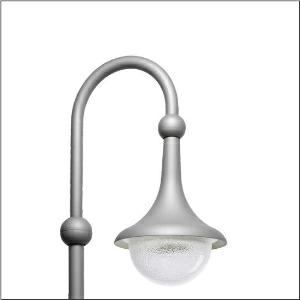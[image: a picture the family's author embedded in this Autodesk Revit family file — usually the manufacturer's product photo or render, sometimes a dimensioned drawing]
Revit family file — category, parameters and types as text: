
# Revit family: kleine_glocke___st1_2a_5xa1573k1b208_586f
name_source: partatom
category: Lighting Fixtures
units: mm (PartAtom-declared; Revit-internal decimal feet)

## family parameters
Cut with Voids When Loaded = No
Host = Face
Light Source = No
Part Type = Normal
Room Calculation Point = No
Round Connector Dimension = Use Diameter
Shared = No

## types (1)
- --- (1 x LED, 1750 lm, 13.2 W, 4000K)
    Apparent Load = 13 VA
    CIE Flux Codes = 28 64 93 98 100
    Color Rendering = 70
    Color Temperature = 4000K
    Default Elevation = 1800 mm
    Description = Small Bell, mast luminaire, primary light control with 3 zone facetted reflector, of plastic, aluminium vaporised, primary optical cover: enclosure, of PMMA, transparent structured, light distribution: ST1.2a, light emission: direct distribution, primary light characteristic: asymmetric, installation type: suspended mounting, LED, High Power LED, rated luminous flux: 1.750lm, luminous efficacy: 133lm/W, light colour: 740, colour temperature: 4000K, control gear: ECG Plus, control: flexible luminous flux parameterisation, time-dependent luminous flux control, constant luminous flux control, digital communication interface, power reduction, electronic power reduction, mains connection: 230..240V, AC, 50/60Hz, start of lifetime: 13W, end of service life: 14W, reduction: 7W, luminaire housing, bell-shaped, of glass-fibre reinforced polyester, coated, Siteco® metallic grey (DB 702S), please order curved mast extension separately, diameter: 430mm, height: 575mm, protection rating (complete): IP54, insulation class (complete): insulation class II (safety insulation), certification: CE, ENEC, VDE, impact resistance: IK07, standard-compliant lighting for roads and squares, packaging unit: 1 piece

Light Distribution: ST1.2a
    Height = 575 mm
    Lamp = 1 x LED
    Lamp Light Flux = 1750 lm
    Lamp Power = 13.2 W
    Lamp count = 1
    Length = 430 mm
    Luminous efficacy = 133 lm/W
    Manufacturer = Siteco
    ModVariant = No
    Model = 5XA1573K1B208
    Number of Poles = 1
    OnlyDefault = Yes
    Power Factor = 1
    Product Name = Kleine Glocke | ST1.2a
    Product group = mast luminaire | pylon annexe
    ProductGroupID = 6201
    Protection Class = Protection class II
    Protection Degree = IP 54
    RLX_Detail_Level = 1
    RLX_Emergency_Light_Flux = 0 lm
    RLX_Emergency_Type = 0
    RLX_Emergency_Type_DB = No
    RlxData = <blob elided: 51989 chars, md5=47b06970>
    Socket = socket
    Standby Power = 0 W
    System Light Flux = 1750 lm
    System Power = 13 W
    Type Comments = factory setting: luminous flux: 100 % | dim-lin: 254 | 249 mA
    Type Image = l_1284392.jpg
    URL = http://relux.com
    VarID = @adj_154303
    Voltage = 0 V
    Weight = 0.00 kg
    Width = 0 mm  [stored 0 ft]

note: [stored X ft] marks values corroborated as IEEE doubles in the binary element streams (Revit-internal decimal feet)

## geometry (parser evidence)
native form markers: Blend x4, Sweep x10
no freeform markers — native parametric forms only
